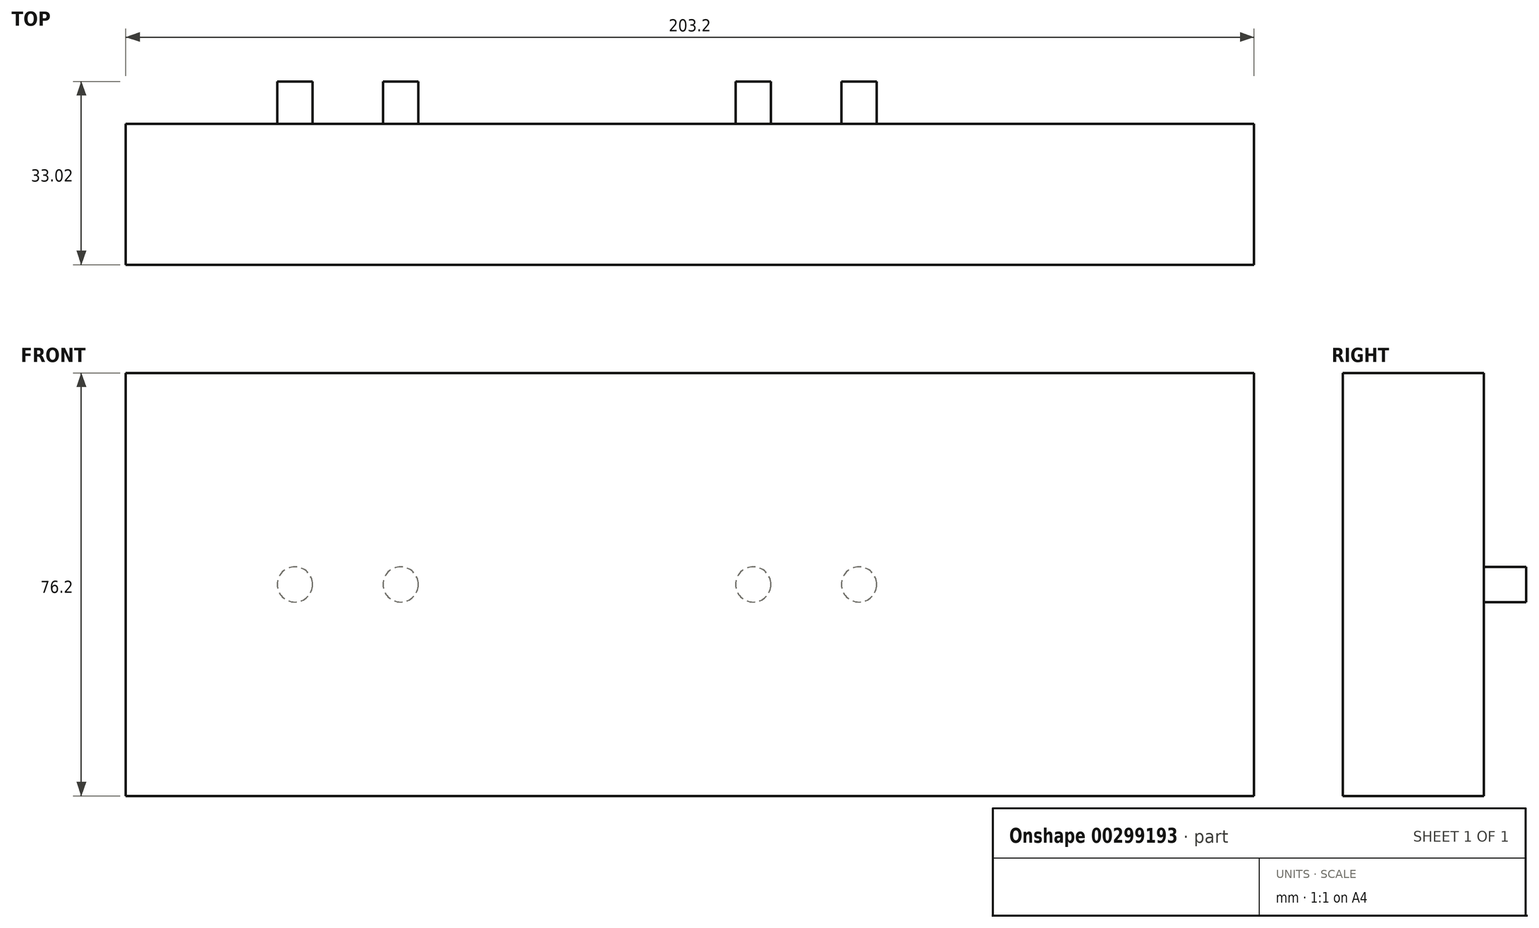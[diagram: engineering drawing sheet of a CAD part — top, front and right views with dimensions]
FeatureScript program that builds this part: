
annotation { "Feature Type Name" : "Feature", "Feature Type Description" : "" }
export const myFeature = defineFeature(function(context is Context, id is Id, definition is map)
    precondition{}
    {
        {
            var Q0;
            Q0=qCreatedBy(makeId("Front.planeOp"),FACE);
            var sketch = newSketch(context, id + "F0", { "sketchPlane" : qUnion([Q0])});
            skLineSegment(sketch, "E0.bottom", {"start": v(0, 0) * mm, "end": v(203.2, 0) * mm});
            skLineSegment(sketch, "E0.top", {"start": v(0, 76.2) * mm, "end": v(203.2, 76.2) * mm});
            skLineSegment(sketch, "E0.left", {"start": v(0, 0) * mm, "end": v(0, 76.2) * mm});
            skLineSegment(sketch, "E0.right", {"start": v(203.2, 0) * mm, "end": v(203.2, 76.2) * mm});
            skLineSegment(sketch, "E1", {"start": v(22, 38.1) * mm, "end": v(0, 38.1) * mm, "construction": true});
            skLineSegment(sketch, "E2", {"start": v(0, 38.1) * mm, "end": v(22, 38.1) * mm, "construction": true});
            skLineSegment(sketch, "E3", {"start": v(203.2, 38.1) * mm, "end": v(22, 38.1) * mm, "construction": true});
            skCircle(sketch, "E4", {"center": v(49.5, 38.1) * mm, "radius": 3.18 * mm});
            skCircle(sketch, "E5", {"center": v(113, 38.1) * mm, "radius": 3.18 * mm});
            skPoint(sketch, "E6.center.orphan", {"position": v(30.46, 38.1) * mm});
            skCircle(sketch, "E7", {"center": v(30.46, 38.1) * mm, "radius": 3.18 * mm});
            skLineSegment(sketch, "E8", {"start": v(113, 38.1) * mm, "end": v(132.06, 38.1) * mm});
            skCircle(sketch, "E9", {"center": v(132.06, 38.1) * mm, "radius": 3.18 * mm});
            skSolve(sketch);
        }
        {
            var Q0;
            Q0 = qSketchRegion(id + "F0", true);
            var Q1;
            Q1=makeQuery(id+"F0.imprint","IMPRINT",FACE,{"disambiguationData":[TD([[makeQuery(id+"F0.imprint","IMPRINT",EDGE,{"derivedFrom":sQuery(id+"F0.wireOp",EDGE,"E9")}),1.0]])]});
            var Q2;
            Q2=makeQuery(id+"F0.imprint","IMPRINT",FACE,{"disambiguationData":[TD([[makeQuery(id+"F0.imprint","IMPRINT",EDGE,{"derivedFrom":sQuery(id+"F0.wireOp",EDGE,"E5")}),1.0]])]});
            var Q3;
            Q3=makeQuery(id+"F0.imprint","IMPRINT",FACE,{"disambiguationData":[TD([[makeQuery(id+"F0.imprint","IMPRINT",EDGE,{"derivedFrom":sQuery(id+"F0.wireOp",EDGE,"E4")}),1.0]])]});
            var Q4;
            Q4=makeQuery(id+"F0.imprint","IMPRINT",FACE,{"disambiguationData":[TD([[makeQuery(id+"F0.imprint","IMPRINT",EDGE,{"derivedFrom":sQuery(id+"F0.wireOp",EDGE,"E7")}),1.0]])]});
            extrude(context, id + "F1", {"entities" : qUnion([Q0, Q1, Q2, Q3, Q4]), "depth" : 25.4 * mm});
        }
        {
            var Q0;
            Q0=makeQuery(id+"F0.imprint","IMPRINT",FACE,{"disambiguationData":[TD([[makeQuery(id+"F0.imprint","IMPRINT",EDGE,{"derivedFrom":sQuery(id+"F0.wireOp",EDGE,"E9")}),1.0]])]});
            var Q1;
            Q1=makeQuery(id+"F0.imprint","IMPRINT",FACE,{"disambiguationData":[TD([[makeQuery(id+"F0.imprint","IMPRINT",EDGE,{"derivedFrom":sQuery(id+"F0.wireOp",EDGE,"E5")}),1.0]])]});
            var Q2;
            Q2=makeQuery(id+"F0.imprint","IMPRINT",FACE,{"disambiguationData":[TD([[makeQuery(id+"F0.imprint","IMPRINT",EDGE,{"derivedFrom":sQuery(id+"F0.wireOp",EDGE,"E4")}),1.0]])]});
            var Q3;
            Q3=makeQuery(id+"F0.imprint","IMPRINT",FACE,{"disambiguationData":[TD([[makeQuery(id+"F0.imprint","IMPRINT",EDGE,{"derivedFrom":sQuery(id+"F0.wireOp",EDGE,"E7")}),1.0]])]});
            extrude(context, id + "F2", {"entities" : qUnion([Q0, Q1, Q2, Q3]), "operationType" : NewBodyOperationType.ADD, "oppositeDirection" : true, "depth" : 7.62 * mm});
        }
    });
